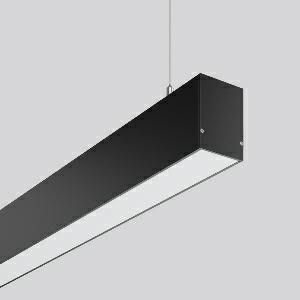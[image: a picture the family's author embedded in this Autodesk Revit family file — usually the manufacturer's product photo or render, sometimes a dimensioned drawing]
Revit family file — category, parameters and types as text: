
# Revit family: less_is_more_50_312319_003_76_c760
name_source: partatom
category: Lighting Fixtures
units: mm (PartAtom-declared; Revit-internal decimal feet)

## family parameters
Cut with Voids When Loaded = No
Host = Face
Light Source = No
Part Type = Normal
Room Calculation Point = No
Round Connector Dimension = Use Diameter
Shared = No

## types (1)
- LESS IS MORE 50 (1 x LED Modul 830, 6150 lm, 3000)
    Apparent Load = 52 VA
    CIE Flux Codes = 49 80 96 63 100
    Color Rendering = 80
    Color Temperature = 3000
    Default Elevation = 1800 mm
    Description = Series: LESS IS MORE 50
Linear pendant luminaire for aesthetically sophisticated lighting. Housing: extruded aluminium profile, powder-coated. End cap aluminium powder-coated. Canopy made of aluminium, powder-coated. Diffuser made of non-yellowing plastic (PMMA), opal. Direct 65%, indirect 35% light emission. Suitable for pendant. 2-point steel cable suspension freely positionable and infinitely height-adjustable. Special lengths available on request. LED unit with integrated converter interchangeable and removable. Suitable for through-wiring. With sensors or as a safety luminaire on request. 
Colour: deep black, matt (RAL 9005)
Length: 1407 mm
Width: 57 mm
Height: 75 mm
Suspension length: 2000 mm
Lamp: LED
Socket: without socket
Colour temperature: 3000K
Colour rendering index (CRI): 80
Light source: LED
Socket lamp2: Without base
Colour temperature: 3000K
System power: 52 W
Rated luminous flux: 6150 lm
Luminous efficiency: 118 lm/W
Control gear: Converter, dimmable, DALI
Control gear: Converter, dimmable, DALI
Protection class: I
Type of protection: IP 20
    Height = 75 mm
    Lamp = 1 x LED Modul 830
    Lamp Light Flux = 6150 lm
    Lamp count = 1
    Length = 1407 mm
    Lifetime = 50000 h
    Luminous efficacy = 118 lm/W
    Manufacturer = RZB
    ModVariant = No
    Model = 312319.003.76
    Mounting Place = Ceiling
    Mounting Type = Pendant
    Number of Poles = 1
    OnlyDefault = Yes
    Power Factor = 1
    Product Name = LESS IS MORE 50
    Product group = Pendant LED linear luminaires
    ProductGroupID = 907
    Protection Class = Protection class I
    Protection Degree = IP 20
    RLX_Detail_Level = 1
    RLX_Emergency_Light_Flux = 0 lm
    RLX_Emergency_Type = 0
    RLX_Emergency_Type_DB = No
    RlxData = <blob elided: 39893 chars, md5=ae262e17>
    Socket = socket
    Standby Power = 0 W
    System Light Flux = 6150 lm
    System Power = 52 W
    Type Comments = Product without accessories
    Type Image = 312318.003.jpg
    URL = http://relux.com
    VarID = ---
    Voltage = 230 V
    Voltage Range = 220-240 V
    Weight = 0.00 kg
    Width = 57 mm

## geometry (parser evidence)
native form markers: Blend x4, Sweep x12
no freeform markers — native parametric forms only
